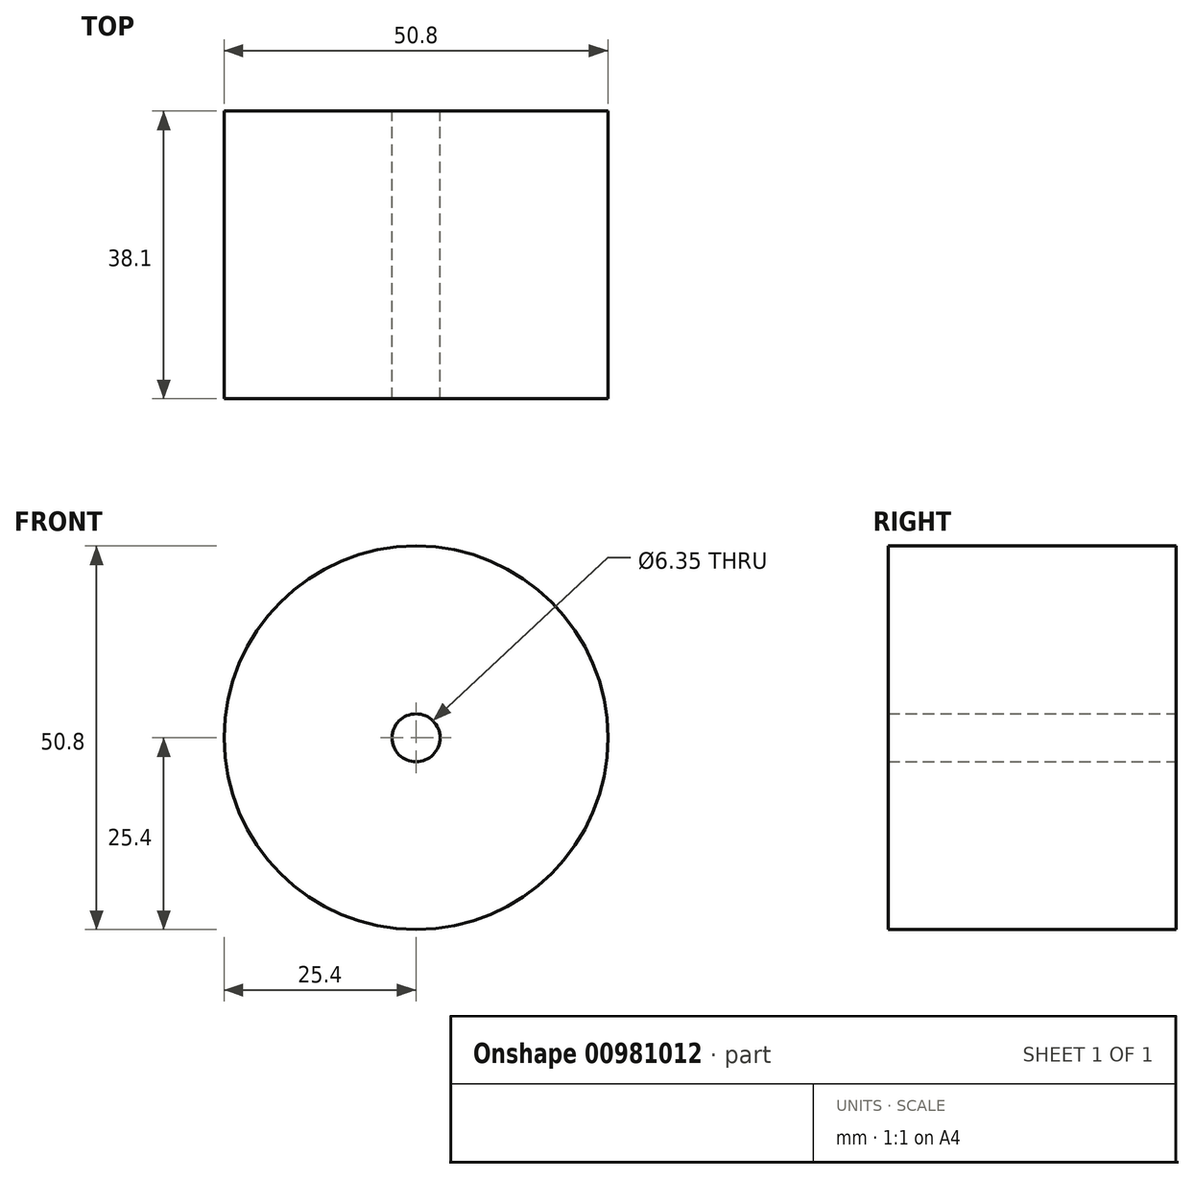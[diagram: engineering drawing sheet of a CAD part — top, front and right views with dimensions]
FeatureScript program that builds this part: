
annotation { "Feature Type Name" : "Feature", "Feature Type Description" : "" }
export const myFeature = defineFeature(function(context is Context, id is Id, definition is map)
    precondition{}
    {
        {
            var Q0;
            Q0=qCreatedBy(makeId("Front.planeOp"),FACE);
            var sketch = newSketch(context, id + "F0", { "sketchPlane" : qUnion([Q0])});
            skCircle(sketch, "E0", {"center": v(0, 0) * mm, "radius": 25.4 * mm});
            skCircle(sketch, "E1", {"center": v(0, 0) * mm, "radius": 3.18 * mm});
            skSolve(sketch);
        }
        {
            var Q0;
            Q0 = qSketchRegion(id + "F0", true);
            extrude(context, id + "F1", {"entities" : qUnion([Q0]), "depth" : 38.1 * mm, "offsetDistance" : 25.4 * mm});
        }
        {
            var Q0;
            Q0=sQuery(id+"F0.wireOp",EDGE,"E1");
            extrude(context, id + "F2", {"bodyType" : ToolBodyType.SURFACE, "surfaceEntities" : qUnion([Q0]), "depth" : 82.55 * mm, "offsetDistance" : 25.4 * mm});
        }
    });
